# Revit family: I8SM+
name_source: partatom
category: Communication Devices
revit_build: Autodesk Revit 2014 (Build: 20130308_1515(x64)
units: mm (PartAtom-declared; Revit-internal decimal feet)

## types (1)
- IP Loudspeaker System
    100V Taps = 32.00 W
    70V Taps = 32.00 W
    Baffle Material = QF_Plastic - Black - Fine Textured
    Body Material = QF_Plastic - White - Smooth
    Color = <By Category>
    Communication Ports = RJ-45
    Cost = 0 $
    Cost MSRP = 0 $
    Coverage = 105° (2kHz Octave Band, -6dB Points
    Coverage Horizontal = 105.00°
    Coverage Vertical = 105.00°
    Depth = 11.5 "
    Description = POE+ INDOOR WALL / CEILING MOUNT IP LOUDSPEAKER WITH PAGING MICROPHONE
    Dispersion Angle = 0.00°
    Enclosure Material = <By Category>
    Family Code (default) = LOUD SPEAKERS
    Frequency Response  = 86Hz - 15.5kHz
    Grill Material = QF_Plastic - Black - Fine Textured
    Height = 2.84 "
    IQ Category = SPEAKERS
    Impedance = 8
    Ingress Protection = IP-30
    Loudspeaker Level = 8Ω, 9W (802.3AF), 15W (802.3AT)
    Manufacturer = ATLAS SOUND
    Manufacturer URL = https://www.atlasied.com
    Market = Commercial, Higher Education, Emergency
    MasterFormat = 27 41 13
    MaterFormat Title = SPEAKERS
    Max Input Ratings (8Ω) = TBD
    Model = I8SM+
    Mount Material = QF_Plastic - White - Smooth
    Mounting/Rigging Provisions = Mounting Enclosure is Not Included (See Optional Enclosure)
    OmniClass Number = 23-37 17 13 19
    OmniClass Title = SPEAKERS
    Operation Mode = Self Powered
    Power Rating (RMS) = 15 Watts Max (802.3AT)
    Product Documentation Link = https://www.atlasied.com
    Product Page URL = https://www.atlasied.com
    Recommended Signal Processing = Built-In Processing
    SPL Max = 106
    Safety Agency Ratings = ETL Listed to Comply with UL-60950-1, and CAN/CSA-C22.2 No. 60950-1
    ScheduleType |RF| = AtlasIED Master
    Speaker Dispersion = 120.00°
    Speaker Type = S1
    Transformer Option = Yes
    URL = www.atlassound.com
    Vertical Symmetry = Yes
    Voltage AC = PoE or PoE+ and External 24VDC
    Warranty = 1 Year
    Weight Product = 3.6
    Width = 0 "

## geometry (parser evidence)
native form markers: Sweep x2
no freeform markers — native parametric forms only
